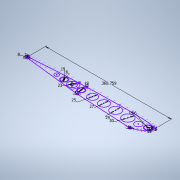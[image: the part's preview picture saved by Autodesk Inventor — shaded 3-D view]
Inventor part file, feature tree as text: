
AUTODESK INVENTOR PART (.ipt)
format: ipt  version: 2022 (Build 260153000, 153)  size: 208,896 bytes
history: native  units: mm
features: sketch x1
ambient origin geometry x8: Origin, YZ Plane, XZ Plane, XY Plane, X Axis, Y Axis, Z Axis, Center Point
feature tree (1):
  sketch  "Sketch1"  dims[d31=34.456mm d50=368.759386mm d57=16.0mm d69=8.0mm d70=23.0mm d71=8.0mm d73=16.0mm d80=19.0mm d81=16.0mm d82=1.0mm d83=1.0mm d84=1.0mm d85=1.0mm d86=1.0mm d87=0.8mm d88=1.0mm d90=19.0mm d94=5.0mm d95=5.0mm d101=5.0mm d102=5.0mm d105=5.0mm d106=5.0mm d108=2.0mm d109=19.0mm d110=30.0mm d111=29.0mm d112=27.0mm d113=25.0mm]
